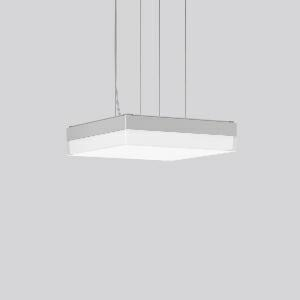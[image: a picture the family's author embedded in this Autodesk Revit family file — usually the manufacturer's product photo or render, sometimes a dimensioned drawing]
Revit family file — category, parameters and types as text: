
# Revit family: flat_slim_square_312542_004_730_de0b
name_source: partatom
category: Lighting Fixtures
units: mm (PartAtom-declared; Revit-internal decimal feet)

## family parameters
Cut with Voids When Loaded = No
Host = Face
Light Source = No
Part Type = Normal
Room Calculation Point = No
Round Connector Dimension = Use Diameter
Shared = No

## types (1)
- MultiLumen 2 840 (1 x LED Modul 840, 2300 lm, 4000)
    Apparent Load = 21 VA
    CIE Flux Codes = 43 75 93 91 100
    Color Rendering = 80
    Color Temperature = 4000
    Default Elevation = 1800 mm
    Height = 70 mm
    Lamp = 1 x LED Modul 840
    Lamp Light Flux = 2300 lm
    Lamp count = 1
    Length = 300 mm
    Lifetime = 50000 h
    Luminous efficacy = 110 lm/W
    Manufacturer = RZB
    ModVariant = No
    Model = 312542.004.730
    Mounting Place = Ceiling
    Mounting Type = Pendant
    Number of Poles = 1
    OnlyDefault = Yes
    Power Factor = 1
    Product Name = FLAT SLIM square
    Product group = Pendant luminaires
    ProductGroupID = 902
    Protection Class = Protection class I
    Protection Degree = IP 40
    RLX_Detail_Level = 1
    RLX_Emergency_Light_Flux = 0 lm
    RLX_Emergency_Type = 0
    RLX_Emergency_Type_DB = No
    RlxData = <blob elided: 14517 chars, md5=1a67e688>
    Socket = socket
    Standby Power = 0 W
    System Light Flux = 2300 lm
    System Power = 21 W
    Type Comments = MultiLumen 2 840
    Type Image = 312542.004.jpg
    URL = http://relux.com
    VarID = multilumen_2_840
    Voltage = 230 V
    Voltage Range = 220-240 V
    Weight = 0.00 kg
    Width = 300 mm

## geometry (parser evidence)
native form markers: Sweep x14
no freeform markers — native parametric forms only
